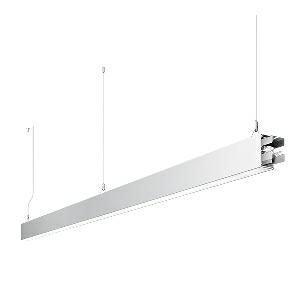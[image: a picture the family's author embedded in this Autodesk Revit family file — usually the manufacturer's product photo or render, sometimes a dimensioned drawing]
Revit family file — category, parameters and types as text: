
# Revit family: idoo_line_-_ilp_6000_vtl_d_sta_00806457_aeba
name_source: partatom
category: Lighting Fixtures
units: mm (PartAtom-declared; Revit-internal decimal feet)

## family parameters
Cut with Voids When Loaded = No
Host = Face
Light Source = No
Part Type = Normal
Room Calculation Point = No
Round Connector Dimension = Use Diameter
Shared = No

## types (1)
- IDOO.line - ILP 6000/VTL/D STA (1 x LED, 6150 lm, 2700-6500K)
    Apparent Load = 63 VA
    Approval mark = CE
    CIE Flux Codes = 66 91 98 40 100
    Color Rendering = 90-100
    Color Temperature = 2700-6500K
    Control Gear = Electronic ballast
    Default Elevation = 1800 mm
    Description = ILP 6000/VTL/D|Suspended luminaire|light source: LED|connected load: 220-240 V, 50/60 Hz|Power consumption: approx. 63 W|standby: approx. 0,25|luminous flux: 6150 lm|luminous efficacy: 97 lm/W|light distribution: Direct/indirect|direct ratio: approx. 40 %|colour temperature: Cold white, ca. 2700-6500 K|color rendering index (CRI): >= 90|chromaticity tolerance:  3 SDCM|System of protection: IP 40|technology: Continuously dimmable|luminaire body|material: Sectional aluminium|colour: White|lamp cover: Acrylic (PMMA), Clear|mains lead: 2.00 m With free stranded wires|Fastening: Steel cable 0.3 - 0.7 m|glare control: Prism aperture|luminance(L65): <= 2700 cd/m|unified glare rating(4H 8H): <=  16|special features: Specified values at approx. 4000 K, DALI Load 1x, Through-wired, up to 18 m on one mains connection, External control required for Dali Device type 8, Flicker-free, Constant luminous flux between 2700 and 6500 K, Constant colour temperature over the whole dimming range, Suitable as emergency lighting, Start luminaire with mains connection, Mechanical and electrical connection of the individual modules without tools|
    Frequency = 50 Hz
    Height = 110 mm
    Lamp = 1 x LED
    Lamp Light Flux = 6150 lm
    Lamp count = 1
    Length = 2250 mm
    Luminous efficacy = 98 lm/W
    Manufacturer = Waldmann
    ModVariant = No
    Model = 00806457
    Mounting Place = Ceiling
    Mounting Type = Pendant
    Number of Poles = 1
    OnlyDefault = Yes
    Power Factor = 1
    Product Name = IDOO.line - ILP 6000/VTL/D STA
    Product group = Suspended luminaire
    ProductGroupID = 9
    Protection Class = Protection class I
    Protection Degree = IP 40
    RLX_Detail_Level = 1
    RLX_Emergency_Light_Flux = 0 lm
    RLX_Emergency_Type = 0
    RLX_Emergency_Type_DB = No
    RlxData = <blob elided: 23301 chars, md5=4a9c933c>
    Socket = socket
    Standby Power = 0 W
    System Light Flux = 6150 lm
    System Power = 63 W
    Type Comments = Product without accessories
    Type Image = 113313000-00692603.jpg
    URL = http://relux.com
    VarID = ---
    Voltage = 230 V
    Voltage Range = 220-240 V
    Weight = 0.00 kg
    Width = 60 mm  [stored 0.19685 ft]

note: [stored X ft] marks values corroborated as IEEE doubles in the binary element streams (Revit-internal decimal feet)

## geometry (parser evidence)
native form markers: Blend x4, Sweep x14
no freeform markers — native parametric forms only
